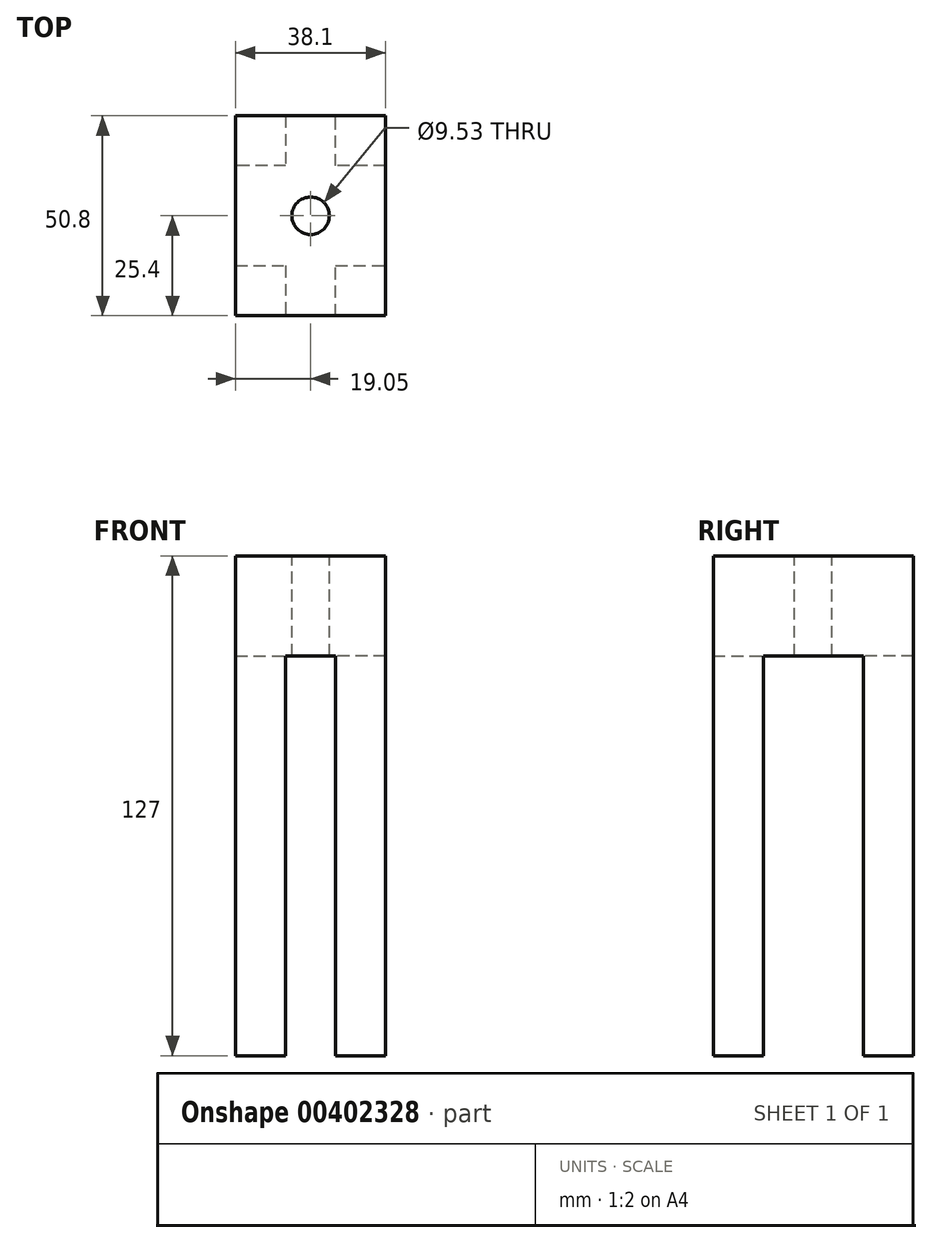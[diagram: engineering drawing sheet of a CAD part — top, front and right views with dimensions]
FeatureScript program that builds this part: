
annotation { "Feature Type Name" : "Feature", "Feature Type Description" : "" }
export const myFeature = defineFeature(function(context is Context, id is Id, definition is map)
    precondition{}
    {
        {
            var Q0;
            Q0=qCreatedBy(makeId("Top.planeOp"),FACE);
            var sketch = newSketch(context, id + "F0", { "sketchPlane" : qUnion([Q0])});
            skLineSegment(sketch, "E0.bottom", {"start": v(-19.05, 25.4) * mm, "end": v(19.05, 25.4) * mm});
            skLineSegment(sketch, "E0.top", {"start": v(-19.05, -25.4) * mm, "end": v(19.05, -25.4) * mm});
            skLineSegment(sketch, "E0.left", {"start": v(-19.05, 25.4) * mm, "end": v(-19.05, -25.4) * mm});
            skLineSegment(sketch, "E0.right", {"start": v(19.05, 25.4) * mm, "end": v(19.05, -25.4) * mm});
            skPoint(sketch, "E0.middle", {"position": v(0, 0) * mm});
            skSolve(sketch);
        }
        {
            var Q0;
            Q0=qSketchRegion(id+"F0",true);
            extrude(context, id + "F1", {"entities" : qUnion([Q0]), "depth" : 127 * mm, "offsetDistance" : 25.4 * mm, "symmetric" : true});
        }
        {
            var Q0;
            Q0=makeQuery(id+"F1.opExtrude","CAP_FACE",FACE,{"disambiguationData":[OSD([sQuery(id+"F0.wireOp",EDGE,"E0.bottom"),sQuery(id+"F0.wireOp",EDGE,"E0.top"),sQuery(id+"F0.wireOp",EDGE,"E0.left"),sQuery(id+"F0.wireOp",EDGE,"E0.right")])],"isStart":true});
            var sketch = newSketch(context, id + "F2", { "sketchPlane" : qUnion([Q0])});
            skLineSegment(sketch, "E1", {"start": v(-6.35, 25.4) * mm, "end": v(6.35, 25.4) * mm});
            skLineSegment(sketch, "E2", {"start": v(6.35, 25.4) * mm, "end": v(6.35, 12.7) * mm});
            skLineSegment(sketch, "E3", {"start": v(6.35, 12.7) * mm, "end": v(19.05, 12.7) * mm});
            skLineSegment(sketch, "E4", {"start": v(19.05, 12.7) * mm, "end": v(19.05, -12.7) * mm});
            skLineSegment(sketch, "E5", {"start": v(19.05, -12.7) * mm, "end": v(6.35, -12.7) * mm});
            skLineSegment(sketch, "E6", {"start": v(6.35, -12.7) * mm, "end": v(6.35, -25.4) * mm});
            skLineSegment(sketch, "E7", {"start": v(6.35, -25.4) * mm, "end": v(-6.35, -25.4) * mm});
            skLineSegment(sketch, "E8", {"start": v(-6.35, -25.4) * mm, "end": v(-6.35, -12.7) * mm});
            skLineSegment(sketch, "E9", {"start": v(-6.35, -12.7) * mm, "end": v(-19.05, -12.7) * mm});
            skLineSegment(sketch, "E10", {"start": v(-19.05, -12.7) * mm, "end": v(-19.05, 12.7) * mm});
            skLineSegment(sketch, "E11", {"start": v(-19.05, 12.7) * mm, "end": v(-6.35, 12.7) * mm});
            skLineSegment(sketch, "E12", {"start": v(-6.35, 12.7) * mm, "end": v(-6.35, 25.4) * mm});
            skSolve(sketch);
        }
        {
            var Q0;
            Q0=qSketchRegion(id+"F2",true);
            extrude(context, id + "F3", {"entities" : qUnion([Q0]), "operationType" : NewBodyOperationType.REMOVE, "oppositeDirection" : true, "depth" : 101.6 * mm, "offsetDistance" : 25.4 * mm});
        }
        {
            var Q0;
            Q0=makeQuery(id+"F1.opExtrude","CAP_FACE",FACE,{"disambiguationData":[OSD([sQuery(id+"F0.wireOp",EDGE,"E0.bottom"),sQuery(id+"F0.wireOp",EDGE,"E0.top"),sQuery(id+"F0.wireOp",EDGE,"E0.left"),sQuery(id+"F0.wireOp",EDGE,"E0.right")])],"isStart":false});
            var sketch = newSketch(context, id + "F4", { "sketchPlane" : qUnion([Q0])});
            skCircle(sketch, "E13", {"center": v(0, 0) * mm, "radius": 4.76 * mm});
            skSolve(sketch);
        }
        {
            var Q0;
            Q0=qSketchRegion(id+"F4",true);
            extrude(context, id + "F5", {"entities" : qUnion([Q0]), "operationType" : NewBodyOperationType.REMOVE, "oppositeDirection" : true, "depth" : 25.4 * mm});
        }
    });
